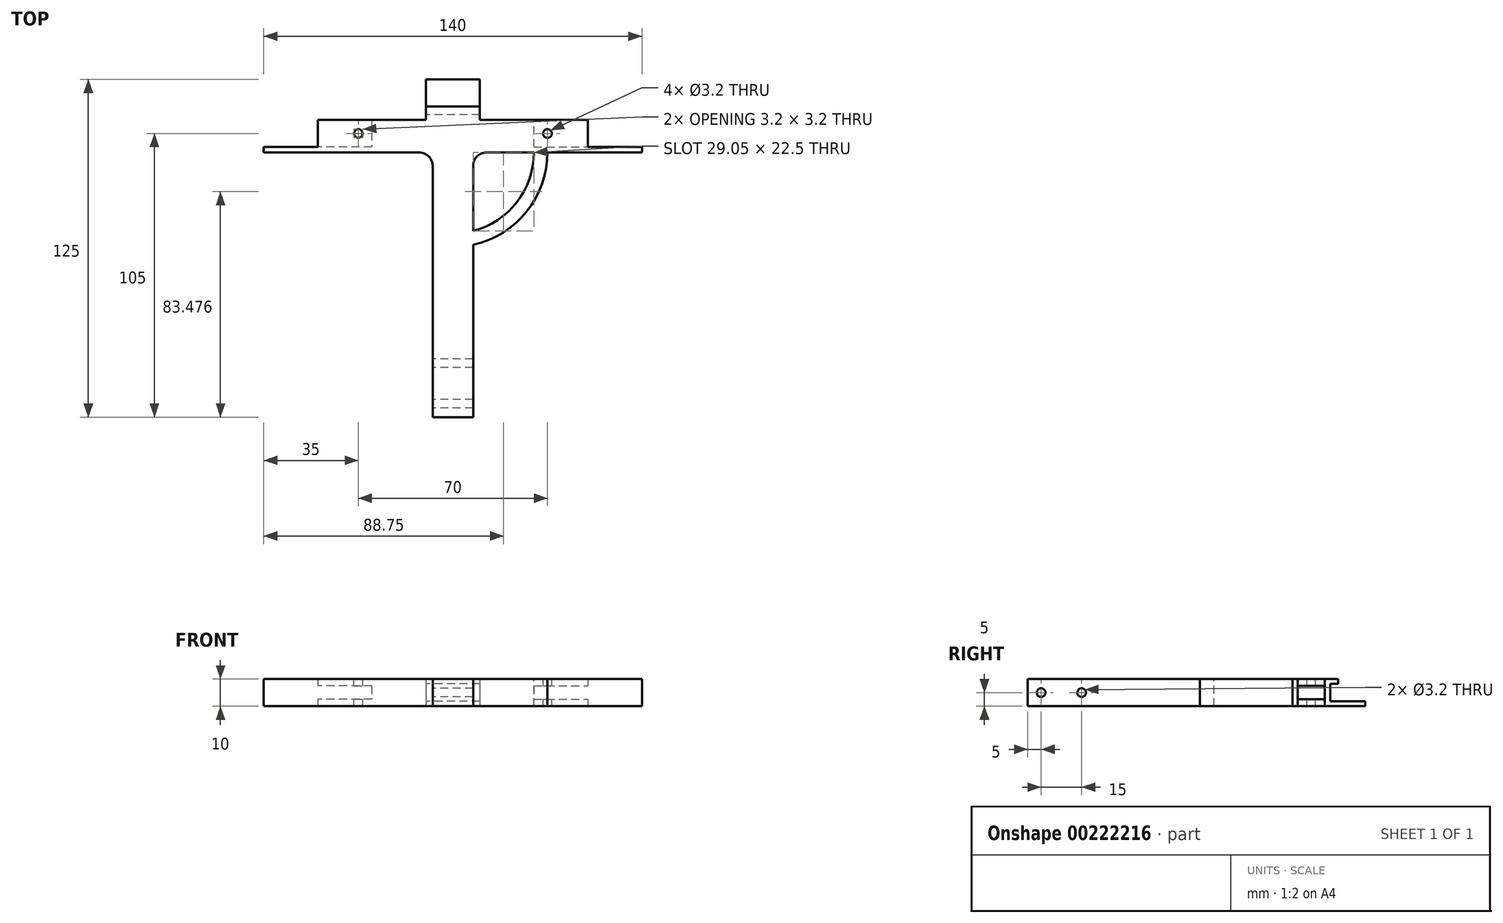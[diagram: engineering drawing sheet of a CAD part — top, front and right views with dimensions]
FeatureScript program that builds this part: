
annotation { "Feature Type Name" : "Feature", "Feature Type Description" : "" }
export const myFeature = defineFeature(function(context is Context, id is Id, definition is map)
    precondition{}
    {
        {
            var Q0;
            Q0=qCreatedBy(makeId("Top.planeOp"),FACE);
            var sketch = newSketch(context, id + "F0", { "sketchPlane" : qUnion([Q0])});
            skLineSegment(sketch, "E0.bottom", {"start": v(-7.5, 50) * mm, "end": v(7.5, 50) * mm});
            skLineSegment(sketch, "E0.top", {"start": v(-7.5, -50) * mm, "end": v(7.5, -50) * mm});
            skLineSegment(sketch, "E0.left", {"start": v(-7.5, 50) * mm, "end": v(-7.5, -50) * mm});
            skLineSegment(sketch, "E0.right", {"start": v(7.5, 50) * mm, "end": v(7.5, -50) * mm});
            skPoint(sketch, "E1", {"position": v(0, 50) * mm});
            skPoint(sketch, "E2", {"position": v(-7.5, 0) * mm});
            skSolve(sketch);
        }
        {
            var Q0;
            Q0=makeQuery(id+"F0.imprint","IMPRINT",FACE,{"disambiguationData":[TD([[makeQuery(id+"F0.imprint","IMPRINT",EDGE,{"derivedFrom":sQuery(id+"F0.wireOp",EDGE,"E0.bottom")}),-1.0]])]});
            extrude(context, id + "F1", {"entities" : qUnion([Q0]), "endBound" : BoundingType.SYMMETRIC, "depth" : 10 * mm});
        }
        {
            var Q0;
            Q0=makeQuery(id+"F1.opExtrude","SWEPT_FACE",FACE,{"disambiguationData":[OSD([sQuery(id+"F0.wireOp",EDGE,"E0.bottom")])]});
            var sketch = newSketch(context, id + "F2", { "sketchPlane" : qUnion([Q0])});
            skLineSegment(sketch, "E3.bottom", {"start": v(-50, 5) * mm, "end": v(50, 5) * mm});
            skLineSegment(sketch, "E3.top", {"start": v(-50, -5) * mm, "end": v(50, -5) * mm});
            skLineSegment(sketch, "E3.left", {"start": v(-50, 5) * mm, "end": v(-50, -5) * mm});
            skLineSegment(sketch, "E3.right", {"start": v(50, 5) * mm, "end": v(50, -5) * mm});
            skPoint(sketch, "E4", {"position": v(-50, 0) * mm});
            skPoint(sketch, "E5", {"position": v(0, 5) * mm});
            skSolve(sketch);
        }
        {
            var Q0;
            Q0=qSketchRegion(id+"F2",true);
            extrude(context, id + "F3", {"entities" : qUnion([Q0]), "operationType" : NewBodyOperationType.ADD, "depth" : 10 * mm});
        }
        {
            var Q0;
            Q0=makeQuery(id+"F3.opExtrude","SWEPT_FACE",FACE,{"disambiguationData":[OSD([sQuery(id+"F2.wireOp",EDGE,"E3.right")])]});
            var sketch = newSketch(context, id + "F4", { "sketchPlane" : qUnion([Q0])});
            skLineSegment(sketch, "E6.bottom", {"start": v(-60, -2.5) * mm, "end": v(-50, -2.5) * mm});
            skLineSegment(sketch, "E6.top", {"start": v(-60, 2.5) * mm, "end": v(-50, 2.5) * mm});
            skLineSegment(sketch, "E6.left", {"start": v(-60, -2.5) * mm, "end": v(-60, 2.5) * mm});
            skLineSegment(sketch, "E6.right", {"start": v(-50, -2.5) * mm, "end": v(-50, 2.5) * mm});
            skPoint(sketch, "E7", {"position": v(-60, 0) * mm});
            skSolve(sketch);
        }
        {
            var Q0;
            Q0=makeQuery(id+"F4.imprint","IMPRINT",FACE,{"disambiguationData":[TD([[makeQuery(id+"F4.imprint","IMPRINT",EDGE,{"derivedFrom":sQuery(id+"F4.wireOp",EDGE,"E6.bottom")}),1.0]])]});
            extrude(context, id + "F5", {"entities" : qUnion([Q0]), "operationType" : NewBodyOperationType.REMOVE, "oppositeDirection" : true, "depth" : 20 * mm});
        }
        {
            var Q0;
            Q0=makeQuery(id+"F3.opExtrude","SWEPT_FACE",FACE,{"disambiguationData":[OSD([sQuery(id+"F2.wireOp",EDGE,"E3.left")])]});
            var sketch = newSketch(context, id + "F6", { "sketchPlane" : qUnion([Q0])});
            skLineSegment(sketch, "E8.bottom", {"start": v(50, 2.5) * mm, "end": v(60, 2.5) * mm});
            skLineSegment(sketch, "E8.top", {"start": v(50, -2.5) * mm, "end": v(60, -2.5) * mm});
            skLineSegment(sketch, "E8.left", {"start": v(50, 2.5) * mm, "end": v(50, -2.5) * mm});
            skLineSegment(sketch, "E8.right", {"start": v(60, 2.5) * mm, "end": v(60, -2.5) * mm});
            skPoint(sketch, "E9", {"position": v(50, 0) * mm});
            skSolve(sketch);
        }
        {
            var Q0;
            Q0=makeQuery(id+"F6.imprint","IMPRINT",FACE,{"disambiguationData":[TD([[makeQuery(id+"F6.imprint","IMPRINT",EDGE,{"derivedFrom":sQuery(id+"F6.wireOp",EDGE,"E8.bottom")}),-1.0]])]});
            extrude(context, id + "F7", {"entities" : qUnion([Q0]), "operationType" : NewBodyOperationType.REMOVE, "oppositeDirection" : true, "depth" : 20 * mm});
        }
        {
            var Q0;
            Q0=makeQuery(id+"F3.boolean.opBoolean","MERGE",FACE,{"derivedFrom":[makeQuery(id+"F1.opExtrude","CAP_FACE",FACE,{"disambiguationData":[OSD([sQuery(id+"F0.wireOp",EDGE,"E0.bottom"),sQuery(id+"F0.wireOp",EDGE,"E0.top"),sQuery(id+"F0.wireOp",EDGE,"E0.left"),sQuery(id+"F0.wireOp",EDGE,"E0.right")])],"isStart":false}),makeQuery(id+"F3.opExtrude","SWEPT_FACE",FACE,{"disambiguationData":[OSD([sQuery(id+"F2.wireOp",EDGE,"E3.bottom")])]})]});
            var sketch = newSketch(context, id + "F8", { "sketchPlane" : qUnion([Q0])});
            skCircle(sketch, "E10", {"center": v(-35, 55) * mm, "radius": 1.6 * mm});
            skCircle(sketch, "E11", {"center": v(35, 55) * mm, "radius": 1.6 * mm});
            skLineSegment(sketch, "E12", {"start": v(-35, 55) * mm, "end": v(35, 55) * mm, "construction": true});
            skPoint(sketch, "E13", {"position": v(0, 55) * mm});
            skPoint(sketch, "E14", {"position": v(-50, 55) * mm});
            skSolve(sketch);
        }
        {
            var Q0;
            Q0=makeQuery(id+"F8.imprint","IMPRINT",FACE,{"disambiguationData":[TD([[makeQuery(id+"F8.imprint","IMPRINT",EDGE,{"derivedFrom":sQuery(id+"F8.wireOp",EDGE,"E10")}),1.0]])]});
            var Q1;
            Q1=makeQuery(id+"F8.imprint","IMPRINT",FACE,{"disambiguationData":[TD([[makeQuery(id+"F8.imprint","IMPRINT",EDGE,{"derivedFrom":sQuery(id+"F8.wireOp",EDGE,"E11")}),1.0]])]});
            var Q2;
            Q2=sQuery(id+"F8.wireOp",EDGE,"E10");
            var Q3;
            Q3=makeQuery(id+"F3.boolean.opBoolean","MERGE",FACE,{"derivedFrom":[makeQuery(id+"F1.opExtrude","CAP_FACE",FACE,{"disambiguationData":[OSD([sQuery(id+"F0.wireOp",EDGE,"E0.bottom"),sQuery(id+"F0.wireOp",EDGE,"E0.top"),sQuery(id+"F0.wireOp",EDGE,"E0.left"),sQuery(id+"F0.wireOp",EDGE,"E0.right")])],"isStart":true}),makeQuery(id+"F3.opExtrude","SWEPT_FACE",FACE,{"disambiguationData":[OSD([sQuery(id+"F2.wireOp",EDGE,"E3.top")])]})]});
            extrude(context, id + "F9", {"entities" : qUnion([Q0, Q1]), "operationType" : NewBodyOperationType.REMOVE, "surfaceEntities" : qUnion([Q2]), "endBound" : BoundingType.UP_TO_SURFACE, "oppositeDirection" : true, "endBoundEntityFace" : qUnion([Q3]), "depth" : 25 * mm});
        }
        {
            var Q0;
            {var subQ0=sQuery(id+"F0.wireOp",EDGE,"E0.left");var subQ4=sQuery(id+"F2.wireOp",EDGE,"E3.bottom");var subQ5=sQuery(id+"F2.wireOp",EDGE,"E3.right");var subQ6=sQuery(id+"F2.wireOp",EDGE,"E3.top");Q0=makeQuery(id+"F3.boolean.opBoolean","SPLIT",FACE,{"disambiguationData":[TD([makeQuery(id+"F1.opExtrude","SWEPT_FACE",FACE,{"disambiguationData":[OSD([subQ0])]})])],"derivedFrom":makeQuery(id+"F3.opExtrude","CAP_FACE",FACE,{"disambiguationData":[OSD([subQ4,subQ6,sQuery(id+"F2.wireOp",EDGE,"E3.left"),subQ5])],"isStart":true})});}
            var sketch = newSketch(context, id + "F10", { "sketchPlane" : qUnion([Q0])});
            skPoint(sketch, "E15.oppositeSnap0", {"position": v(-28.75, -5) * mm});
            skLineSegment(sketch, "E15.bottom", {"start": v(-70, 5) * mm, "end": v(70, 5) * mm});
            skLineSegment(sketch, "E15.top", {"start": v(-70, -5) * mm, "end": v(70, -5) * mm});
            skLineSegment(sketch, "E15.left", {"start": v(-70, 5) * mm, "end": v(-70, -5) * mm});
            skLineSegment(sketch, "E15.right", {"start": v(70, 5) * mm, "end": v(70, -5) * mm});
            skPoint(sketch, "E16", {"position": v(0, 5) * mm});
            skSolve(sketch);
        }
        {
            var Q0;
            {var subQ2=sQuery(id+"F10.wireOp",EDGE,"E15.right");Q0=makeQuery(id+"F10.imprint","IMPRINT",FACE,{"disambiguationData":[TD([[makeQuery(id+"F10.imprint","IMPRINT",EDGE,{"derivedFrom":subQ2}),-1.0]])]});}
            var Q1;
            Q1=qSketchRegion(id+"F10",true);
            extrude(context, id + "F11", {"entities" : qUnion([Q0, Q1]), "operationType" : NewBodyOperationType.ADD, "depth" : 2 * mm});
        }
        {
            var Q0;
            Q0=makeQuery(id+"F11.boolean.opBoolean","INTERSECT",EDGE,{"derivedFrom":[makeQuery(id+"F1.opExtrude","SWEPT_FACE",FACE,{"disambiguationData":[OSD([sQuery(id+"F0.wireOp",EDGE,"E0.left")])]}),makeQuery(id+"F11.opExtrude","CAP_FACE",FACE,{"disambiguationData":[OSD([sQuery(id+"F10.wireOp",EDGE,"E15.bottom"),sQuery(id+"F10.wireOp",EDGE,"E15.top"),sQuery(id+"F10.wireOp",EDGE,"E15.left"),sQuery(id+"F10.wireOp",EDGE,"E15.right")])],"isStart":false})]});
            var Q1;
            Q1=makeQuery(id+"F11.boolean.opBoolean","INTERSECT",EDGE,{"derivedFrom":[makeQuery(id+"F1.opExtrude","SWEPT_FACE",FACE,{"disambiguationData":[OSD([sQuery(id+"F0.wireOp",EDGE,"E0.right")])]}),makeQuery(id+"F11.opExtrude","CAP_FACE",FACE,{"disambiguationData":[OSD([sQuery(id+"F10.wireOp",EDGE,"E15.bottom"),sQuery(id+"F10.wireOp",EDGE,"E15.top"),sQuery(id+"F10.wireOp",EDGE,"E15.left"),sQuery(id+"F10.wireOp",EDGE,"E15.right")])],"isStart":false})]});
            fillet(context, id + "F12", {"entities" : qUnion([Q0, Q1]), "radius" : 5 * mm, "tangentPropagation" : true, "allowEdgeOverflow" : false});
        }
        {
            var Q0;
            Q0=makeQuery(id+"F1.opExtrude","SWEPT_FACE",FACE,{"disambiguationData":[OSD([sQuery(id+"F0.wireOp",EDGE,"E0.left")])]});
            var sketch = newSketch(context, id + "F13", { "sketchPlane" : qUnion([Q0])});
            skCircle(sketch, "E17", {"center": v(45, 0) * mm, "radius": 1.6 * mm});
            skCircle(sketch, "E18", {"center": v(30, 0) * mm, "radius": 1.6 * mm});
            skSolve(sketch);
        }
        {
            var Q0;
            Q0=makeQuery(id+"F13.imprint","IMPRINT",FACE,{"disambiguationData":[TD([[makeQuery(id+"F13.imprint","IMPRINT",EDGE,{"derivedFrom":sQuery(id+"F13.wireOp",EDGE,"E18")}),1.0]])]});
            var Q1;
            Q1=makeQuery(id+"F13.imprint","IMPRINT",FACE,{"disambiguationData":[TD([[makeQuery(id+"F13.imprint","IMPRINT",EDGE,{"derivedFrom":sQuery(id+"F13.wireOp",EDGE,"E17")}),1.0]])]});
            extrude(context, id + "F14", {"entities" : qUnion([Q0, Q1]), "operationType" : NewBodyOperationType.REMOVE, "endBound" : BoundingType.UP_TO_NEXT, "oppositeDirection" : true, "depth" : 25 * mm});
        }
        {
            var Q0;
            Q0=makeQuery(id+"F3.opExtrude","CAP_FACE",FACE,{"disambiguationData":[OSD([sQuery(id+"F2.wireOp",EDGE,"E3.bottom"),sQuery(id+"F2.wireOp",EDGE,"E3.top"),sQuery(id+"F2.wireOp",EDGE,"E3.left"),sQuery(id+"F2.wireOp",EDGE,"E3.right")])],"isStart":false});
            var sketch = newSketch(context, id + "F15", { "sketchPlane" : qUnion([Q0])});
            skLineSegment(sketch, "E19.bottom", {"start": v(-10, 5) * mm, "end": v(10, 5) * mm});
            skLineSegment(sketch, "E19.top", {"start": v(-10, -5) * mm, "end": v(10, -5) * mm});
            skLineSegment(sketch, "E19.left", {"start": v(-10, 5) * mm, "end": v(-10, -5) * mm});
            skLineSegment(sketch, "E19.right", {"start": v(10, 5) * mm, "end": v(10, -5) * mm});
            skPoint(sketch, "E20", {"position": v(0, 5) * mm});
            skSolve(sketch);
        }
        {
            var Q0;
            Q0=makeQuery(id+"F15.imprint","IMPRINT",FACE,{"disambiguationData":[TD([[makeQuery(id+"F15.imprint","IMPRINT",EDGE,{"derivedFrom":sQuery(id+"F15.wireOp",EDGE,"E19.bottom")}),-1.0]])]});
            extrude(context, id + "F16", {"entities" : qUnion([Q0]), "operationType" : NewBodyOperationType.ADD, "depth" : 5 * mm});
        }
        {
            var Q0;
            Q0=makeQuery(id+"F16.opExtrude","CAP_FACE",FACE,{"disambiguationData":[OSD([sQuery(id+"F15.wireOp",EDGE,"E19.bottom"),sQuery(id+"F15.wireOp",EDGE,"E19.top"),sQuery(id+"F15.wireOp",EDGE,"E19.left"),sQuery(id+"F15.wireOp",EDGE,"E19.right")])],"isStart":false});
            var sketch = newSketch(context, id + "F17", { "sketchPlane" : qUnion([Q0])});
            skLineSegment(sketch, "E21.bottom", {"start": v(-10, 3.25) * mm, "end": v(10, 3.25) * mm});
            skLineSegment(sketch, "E21.top", {"start": v(-10, -3.25) * mm, "end": v(10, -3.25) * mm});
            skLineSegment(sketch, "E21.left", {"start": v(-10, 3.25) * mm, "end": v(-10, -3.25) * mm});
            skLineSegment(sketch, "E21.right", {"start": v(10, 3.25) * mm, "end": v(10, -3.25) * mm});
            skPoint(sketch, "E22", {"position": v(-10, 0) * mm});
            skSolve(sketch);
        }
        {
            var Q0;
            Q0=makeQuery(id+"F17.imprint","IMPRINT",FACE,{"disambiguationData":[TD([[makeQuery(id+"F17.imprint","IMPRINT",EDGE,{"derivedFrom":sQuery(id+"F17.wireOp",EDGE,"E21.bottom")}),-1.0]])]});
            extrude(context, id + "F18", {"entities" : qUnion([Q0]), "operationType" : NewBodyOperationType.REMOVE, "oppositeDirection" : true, "depth" : 3 * mm});
        }
        {
            var Q0;
            {var subQ0=sQuery(id+"F15.wireOp",EDGE,"E19.top");var subQ1=sQuery(id+"F15.wireOp",EDGE,"E19.left");var subQ2=sQuery(id+"F15.wireOp",EDGE,"E19.right");Q0=makeQuery(id+"F18.boolean.opBoolean","SPLIT",FACE,{"disambiguationData":[TD([makeQuery(id+"F3.opExtrude","SWEPT_FACE",FACE,{"disambiguationData":[OSD([sQuery(id+"F2.wireOp",EDGE,"E3.top")])]})])],"derivedFrom":makeQuery(id+"F16.opExtrude","CAP_FACE",FACE,{"disambiguationData":[OSD([sQuery(id+"F15.wireOp",EDGE,"E19.bottom"),subQ0,subQ1,subQ2])],"isStart":false})});}
            extrude(context, id + "F19", {"entities" : qUnion([Q0]), "operationType" : NewBodyOperationType.ADD, "depth" : 10 * mm});
        }
        {
            var Q0;
            Q0=makeQuery(id+"F16.boolean.opBoolean","MERGE",FACE,{"derivedFrom":[makeQuery(id+"F11.boolean.opBoolean","MERGE",FACE,{"derivedFrom":[makeQuery(id+"F3.boolean.opBoolean","MERGE",FACE,{"derivedFrom":[makeQuery(id+"F1.opExtrude","CAP_FACE",FACE,{"disambiguationData":[OSD([sQuery(id+"F0.wireOp",EDGE,"E0.bottom"),sQuery(id+"F0.wireOp",EDGE,"E0.top"),sQuery(id+"F0.wireOp",EDGE,"E0.left"),sQuery(id+"F0.wireOp",EDGE,"E0.right")])],"isStart":false}),makeQuery(id+"F3.opExtrude","SWEPT_FACE",FACE,{"disambiguationData":[OSD([sQuery(id+"F2.wireOp",EDGE,"E3.bottom")])]})]}),makeQuery(id+"F11.opExtrude","SWEPT_FACE",FACE,{"disambiguationData":[OSD([sQuery(id+"F10.wireOp",EDGE,"E15.bottom")])]})]}),makeQuery(id+"F16.opExtrude","SWEPT_FACE",FACE,{"disambiguationData":[OSD([sQuery(id+"F15.wireOp",EDGE,"E19.bottom")])]})]});
            var sketch = newSketch(context, id + "F20", { "sketchPlane" : qUnion([Q0])});
            skArc(sketch, "E23", {"start": v(30, 48) * mm, "mid": v(21.21, 26.79) * mm, "end": v(0, 18) * mm});
            skArc(sketch, "E24", {"start": v(35, 48) * mm, "mid": v(24.75, 23.25) * mm, "end": v(0, 13) * mm});
            skLineSegment(sketch, "E25", {"start": v(0, 18) * mm, "end": v(0, 13) * mm});
            skLineSegment(sketch, "E26", {"start": v(30, 48) * mm, "end": v(35, 48) * mm});
            skSolve(sketch);
        }
        {
            var Q0;
            {var subQ0=sQuery(id+"F20.wireOp",EDGE,"E26");Q0=makeQuery(id+"F20.imprint","IMPRINT",FACE,{"disambiguationData":[TD([[makeQuery(id+"F20.imprint","IMPRINT",EDGE,{"derivedFrom":subQ0}),-1.0]])]});}
            var Q1;
            {var subQ0=sQuery(id+"F15.wireOp",EDGE,"E19.top");Q1=makeQuery(id+"F19.boolean.opBoolean","MERGE",FACE,{"derivedFrom":[makeQuery(id+"F16.boolean.opBoolean","MERGE",FACE,{"derivedFrom":[makeQuery(id+"F11.boolean.opBoolean","MERGE",FACE,{"derivedFrom":[makeQuery(id+"F3.boolean.opBoolean","MERGE",FACE,{"derivedFrom":[makeQuery(id+"F1.opExtrude","CAP_FACE",FACE,{"disambiguationData":[OSD([sQuery(id+"F0.wireOp",EDGE,"E0.bottom"),sQuery(id+"F0.wireOp",EDGE,"E0.top"),sQuery(id+"F0.wireOp",EDGE,"E0.left"),sQuery(id+"F0.wireOp",EDGE,"E0.right")])],"isStart":true}),makeQuery(id+"F3.opExtrude","SWEPT_FACE",FACE,{"disambiguationData":[OSD([sQuery(id+"F2.wireOp",EDGE,"E3.top")])]})]}),makeQuery(id+"F11.opExtrude","SWEPT_FACE",FACE,{"disambiguationData":[OSD([sQuery(id+"F10.wireOp",EDGE,"E15.top")])]})]}),makeQuery(id+"F16.opExtrude","SWEPT_FACE",FACE,{"disambiguationData":[OSD([subQ0])]})]}),makeQuery(id+"F19.opExtrude","SWEPT_FACE",FACE,{"disambiguationData":[OSD([subQ0])]})]});}
            extrude(context, id + "F21", {"entities" : qUnion([Q0]), "operationType" : NewBodyOperationType.ADD, "endBound" : BoundingType.UP_TO_SURFACE, "oppositeDirection" : true, "endBoundEntityFace" : qUnion([Q1]), "depth" : 25 * mm});
        }
    });
